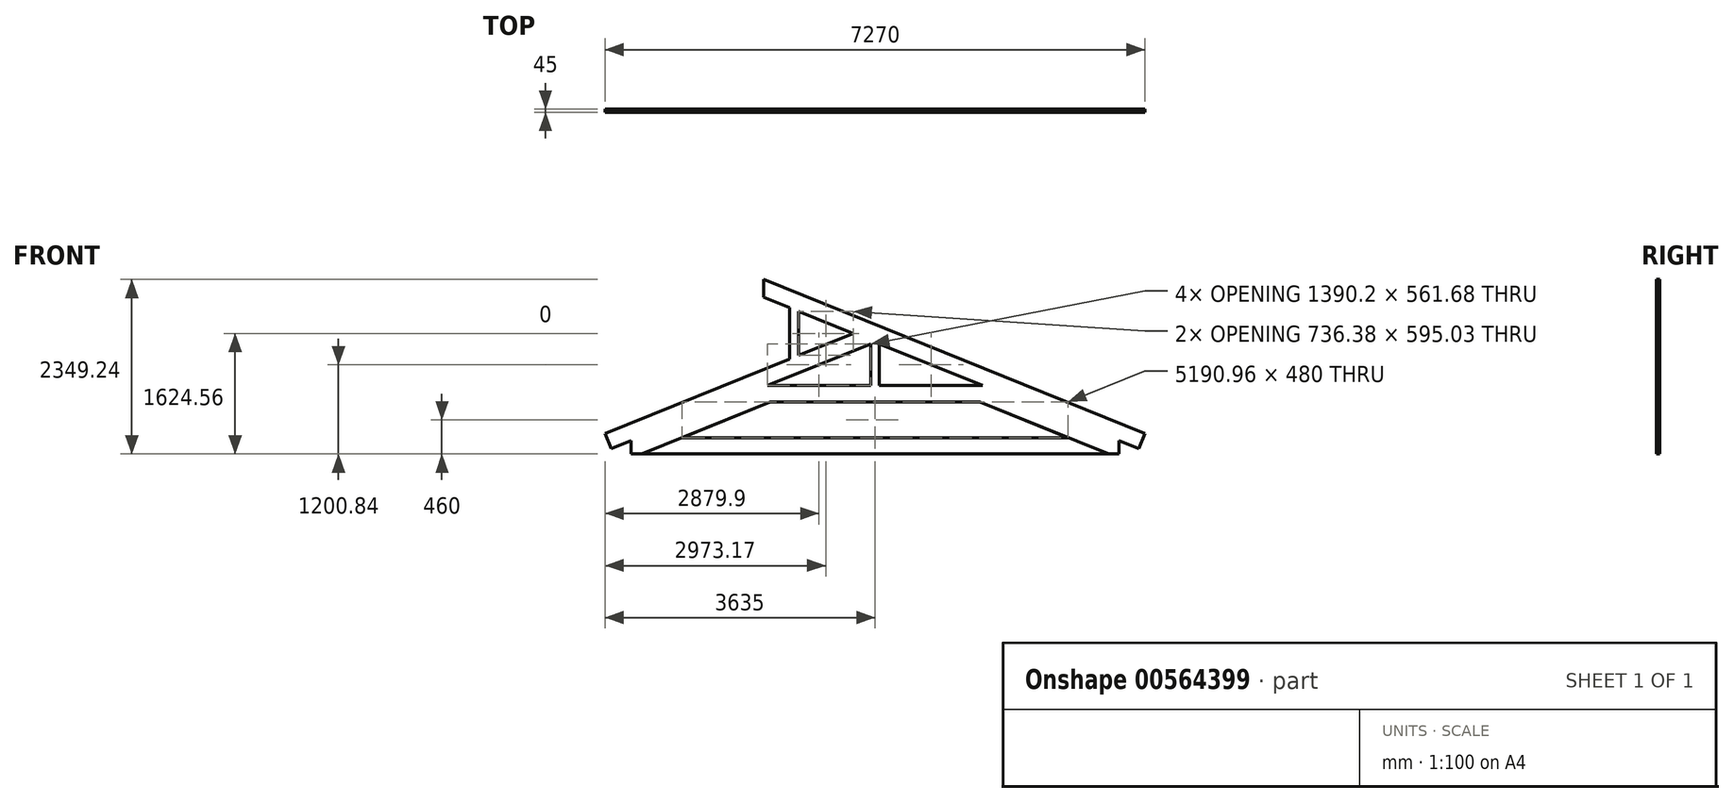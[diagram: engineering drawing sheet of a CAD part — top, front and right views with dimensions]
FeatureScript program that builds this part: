
annotation { "Feature Type Name" : "Feature", "Feature Type Description" : "" }
export const myFeature = defineFeature(function(context is Context, id is Id, definition is map)
    precondition{}
    {
        {
            var Q0;
            Q0=qCreatedBy(makeId("Front.planeOp"),FACE);
            var sketch = newSketch(context, id + "F0", { "sketchPlane" : qUnion([Q0])});
            skLineSegment(sketch, "E0", {"start": v(-3500, 0) * mm, "end": v(3500, 0) * mm, "construction": true});
            skLineSegment(sketch, "E1", {"start": v(-3140, 0) * mm, "end": v(-1407.44, 700) * mm});
            skLineSegment(sketch, "E2", {"start": v(0, 1268.64) * mm, "end": v(3140, 0) * mm, "construction": true});
            skLineSegment(sketch, "E3", {"start": v(-3552.59, 70.58) * mm, "end": v(0, 1505.92) * mm});
            skLineSegment(sketch, "E4", {"start": v(-3140, 0) * mm, "end": v(-3285, 0) * mm});
            skLineSegment(sketch, "E5", {"start": v(-3285, 0) * mm, "end": v(-3285, 178.7) * mm});
            skLineSegment(sketch, "E6", {"start": v(-293.64, 1624.56) * mm, "end": v(-3635, 274.56) * mm});
            skLineSegment(sketch, "E7", {"start": v(-3635, 274.56) * mm, "end": v(-3552.59, 70.58) * mm});
            skLineSegment(sketch, "E8", {"start": v(-1994.72, 700) * mm, "end": v(-1407.44, 700) * mm});
            skLineSegment(sketch, "E9", {"start": v(-1407.44, 700) * mm, "end": v(1994.72, 700) * mm});
            skLineSegment(sketch, "E10", {"start": v(-1450.2, 920) * mm, "end": v(1450.2, 920) * mm});
            skLineSegment(sketch, "E11", {"start": v(3552.59, 70.58) * mm, "end": v(-1500, 2111.96) * mm});
            skPoint(sketch, "E12.orphan", {"position": v(0, 1743.2) * mm});
            skLineSegment(sketch, "E13", {"start": v(3140, 0) * mm, "end": v(1407.44, 700) * mm});
            skLineSegment(sketch, "E14", {"start": v(3140, 0) * mm, "end": v(3285, 0) * mm});
            skLineSegment(sketch, "E15", {"start": v(3285, 0) * mm, "end": v(3285, 178.7) * mm});
            skLineSegment(sketch, "E16", {"start": v(3635, 274.56) * mm, "end": v(-1500, 2349.24) * mm});
            skLineSegment(sketch, "E17", {"start": v(3635, 274.56) * mm, "end": v(3552.59, 70.58) * mm});
            skLineSegment(sketch, "E18", {"start": v(-1500, 2349.24) * mm, "end": v(-1500, 2111.96) * mm});
            skLineSegment(sketch, "E19", {"start": v(-1150.02, 1970.56) * mm, "end": v(-1150.02, 1278.56) * mm});
            skLineSegment(sketch, "E20", {"start": v(-1030.02, 1922.08) * mm, "end": v(-1030.02, 1327.04) * mm});
            skLineSegment(sketch, "E21", {"start": v(-60, 1481.68) * mm, "end": v(-60, 920) * mm});
            skLineSegment(sketch, "E22", {"start": v(60, 920) * mm, "end": v(60, 1481.68) * mm});
            skLineSegment(sketch, "E23", {"start": v(-3140, 0) * mm, "end": v(3140, 0) * mm});
            skLineSegment(sketch, "E24", {"start": v(-2595.48, 220) * mm, "end": v(2595.48, 220) * mm});
            skSolve(sketch);
        }
        {
            var Q0;
            Q0=makeQuery(id+"F0.imprint","IMPRINT",FACE,{"disambiguationData":[TD([[makeQuery(id+"F0.imprint","IMPRINT",EDGE,{"derivedFrom":sQuery(id+"F0.wireOp",EDGE,"E16")}),1.0]])]});
            var Q1;
            {var subQ0=sQuery(id+"F0.wireOp",EDGE,"E19");Q1=makeQuery(id+"F0.imprint","IMPRINT",FACE,{"disambiguationData":[TD([[makeQuery(id+"F0.imprint","IMPRINT",EDGE,{"derivedFrom":subQ0}),1.0]])]});}
            var Q2;
            {var subQ5=sQuery(id+"F0.wireOp",EDGE,"E7");Q2=makeQuery(id+"F0.imprint","IMPRINT",FACE,{"disambiguationData":[TD([[makeQuery(id+"F0.imprint","IMPRINT",EDGE,{"derivedFrom":subQ5}),1.0]])]});}
            var Q3;
            {var subQ0=sQuery(id+"F0.wireOp",EDGE,"E4");Q3=makeQuery(id+"F0.imprint","IMPRINT",FACE,{"disambiguationData":[TD([[makeQuery(id+"F0.imprint","IMPRINT",EDGE,{"derivedFrom":subQ0}),-1.0]])]});}
            var Q4;
            {var subQ4=sQuery(id+"F0.wireOp",EDGE,"E8");Q4=makeQuery(id+"F0.imprint","IMPRINT",FACE,{"disambiguationData":[TD([[makeQuery(id+"F0.imprint","IMPRINT",EDGE,{"derivedFrom":subQ4}),1.0]])]});}
            var Q5;
            {var subQ4=sQuery(id+"F0.wireOp",EDGE,"E21");Q5=makeQuery(id+"F0.imprint","IMPRINT",FACE,{"disambiguationData":[TD([[makeQuery(id+"F0.imprint","IMPRINT",EDGE,{"derivedFrom":subQ4}),1.0]])]});}
            var Q6;
            {var subQ4=sQuery(id+"F0.wireOp",EDGE,"E14");Q6=makeQuery(id+"F0.imprint","IMPRINT",FACE,{"disambiguationData":[TD([[makeQuery(id+"F0.imprint","IMPRINT",EDGE,{"derivedFrom":subQ4}),1.0]])]});}
            extrude(context, id + "F1", {"entities" : qUnion([Q0, Q1, Q2, Q3, Q4, Q5, Q6]), "depth" : 45 * mm, "offsetDistance" : 25 * mm});
        }
        {
            var Q0;
            {var subQ0=sQuery(id+"F0.wireOp",EDGE,"E23");Q0=makeQuery(id+"F0.imprint","IMPRINT",FACE,{"disambiguationData":[TD([[makeQuery(id+"F0.imprint","IMPRINT",EDGE,{"derivedFrom":subQ0}),1.0]])]});}
            var Q1;
            {var subQ4=sQuery(id+"F0.wireOp",EDGE,"E14");Q1=makeQuery(id+"F0.imprint","IMPRINT",FACE,{"disambiguationData":[TD([[makeQuery(id+"F0.imprint","IMPRINT",EDGE,{"derivedFrom":subQ4}),1.0]])]});}
            var Q2;
            Q2=makeQuery(id+"F0.imprint","IMPRINT",FACE,{"disambiguationData":[TD([[makeQuery(id+"F0.imprint","IMPRINT",EDGE,{"derivedFrom":sQuery(id+"F0.wireOp",EDGE,"E16")}),1.0]])]});
            var Q3;
            {var subQ4=sQuery(id+"F0.wireOp",EDGE,"E8");Q3=makeQuery(id+"F0.imprint","IMPRINT",FACE,{"disambiguationData":[TD([[makeQuery(id+"F0.imprint","IMPRINT",EDGE,{"derivedFrom":subQ4}),1.0]])]});}
            var Q4;
            {var subQ4=sQuery(id+"F0.wireOp",EDGE,"E21");Q4=makeQuery(id+"F0.imprint","IMPRINT",FACE,{"disambiguationData":[TD([[makeQuery(id+"F0.imprint","IMPRINT",EDGE,{"derivedFrom":subQ4}),1.0]])]});}
            var Q5;
            {var subQ5=sQuery(id+"F0.wireOp",EDGE,"E7");Q5=makeQuery(id+"F0.imprint","IMPRINT",FACE,{"disambiguationData":[TD([[makeQuery(id+"F0.imprint","IMPRINT",EDGE,{"derivedFrom":subQ5}),1.0]])]});}
            var Q6;
            {var subQ0=sQuery(id+"F0.wireOp",EDGE,"E19");Q6=makeQuery(id+"F0.imprint","IMPRINT",FACE,{"disambiguationData":[TD([[makeQuery(id+"F0.imprint","IMPRINT",EDGE,{"derivedFrom":subQ0}),1.0]])]});}
            var Q7;
            {var subQ0=sQuery(id+"F0.wireOp",EDGE,"E4");Q7=makeQuery(id+"F0.imprint","IMPRINT",FACE,{"disambiguationData":[TD([[makeQuery(id+"F0.imprint","IMPRINT",EDGE,{"derivedFrom":subQ0}),-1.0]])]});}
            extrude(context, id + "F2", {"entities" : qUnion([Q0, Q1, Q2, Q3, Q4, Q5, Q6, Q7]), "depth" : 45 * mm, "offsetDistance" : 25 * mm});
        }
    });
